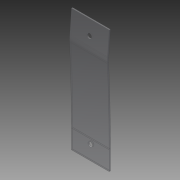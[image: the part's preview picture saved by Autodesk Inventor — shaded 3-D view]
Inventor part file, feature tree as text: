
AUTODESK INVENTOR PART (.ipt)
format: ipt  version: 2014 SP1 (Build 180222100, 222)  size: 126,464 bytes
history: native  units: in
note: dims shown in document units (in); Inventor stores cm internally (conversion verified against a paired STEP export)
features: extrude x5, sketch x4, plane x1
ambient origin geometry x8: Origin, YZ Plane, XZ Plane, XY Plane, X Axis, Y Axis, Z Axis, Center Point
bodies: Solid1 (feature_tree)
feature tree (10):
  extrude  "Extrusion1"  Depth=1.0in
  plane  "Work Plane1"
  sketch  "Sketch2"  dims[d2=0.125in d3=0.375in]
  extrude  "Extrusion2"  Depth=0.375in
  extrude  "Extrusion3"  Depth=0.0312in TaperAngle=0.0deg
  extrude  "Extrusion4"  Depth=1.0in
  extrude  "Extrusion5"  Depth=1.0in
  sketch  "Sketch1"  dims[d0=1.0in d1=3.25in]
  sketch  "Sketch3"  dims[d4=0.375in d5=0.0312in d6=0.0in]
  sketch  "Sketch4"  dims[d7=0.5892in d8=0.75in d9=0.5in d11=0.0312in d12=0.0312in d15=4.0in d16=5.0in d17=1.0in d18=1.0in d19=0.0in d20=1.0in d21=0.0in d22=0.125in d23=0.375in d24=1.0in d25=0.0in d26=0.125in d27=0.375in d28=1.0in d29=0.0in d30=0.125in]
